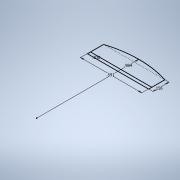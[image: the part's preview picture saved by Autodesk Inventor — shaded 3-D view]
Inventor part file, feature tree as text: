
AUTODESK INVENTOR PART (.ipt)
format: ipt  version: 2021 (Build 250183000, 183)  size: 90,112 bytes
history: native  units: in
note: dims shown in document units (in); Inventor stores cm internally (conversion verified against a paired STEP export)
features: sketch x1
ambient origin geometry x8: Origin, YZ Plane, XZ Plane, XY Plane, X Axis, Y Axis, Z Axis, Center Point
feature tree (1):
  sketch  "Sketch1"  dims[d0=0.9843in d1=0.0295in d2=0.5906in d3=0.1555in]
